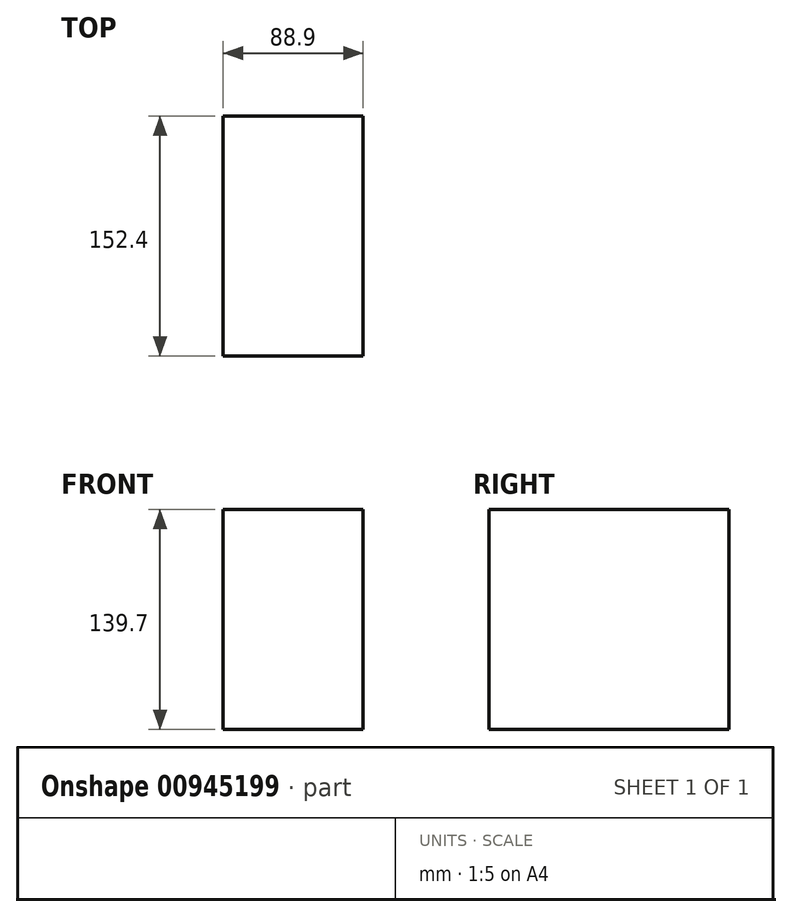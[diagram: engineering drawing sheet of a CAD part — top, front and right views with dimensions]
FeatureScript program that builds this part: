
annotation { "Feature Type Name" : "Feature", "Feature Type Description" : "" }
export const myFeature = defineFeature(function(context is Context, id is Id, definition is map)
    precondition{}
    {
        {
            var Q0;
            Q0=qCreatedBy(makeId("Top.planeOp"),FACE);
            var sketch = newSketch(context, id + "F0", { "sketchPlane" : qUnion([Q0])});
            skLineSegment(sketch, "E0.bottom", {"start": v(-171.68, 124.72) * mm, "end": v(-82.78, 124.72) * mm});
            skLineSegment(sketch, "E0.top", {"start": v(-171.68, -27.68) * mm, "end": v(-82.78, -27.68) * mm});
            skLineSegment(sketch, "E0.left", {"start": v(-171.68, 124.72) * mm, "end": v(-171.68, -27.68) * mm});
            skLineSegment(sketch, "E0.right", {"start": v(-82.78, 124.72) * mm, "end": v(-82.78, -27.68) * mm});
            skSolve(sketch);
        }
        {
            var Q0;
            Q0=makeQuery(id+"F0.imprint","IMPRINT",FACE,{"disambiguationData":[TD([[makeQuery(id+"F0.imprint","IMPRINT",EDGE,{"derivedFrom":sQuery(id+"F0.wireOp",EDGE,"E0.bottom")}),-1.0]])]});
            extrude(context, id + "F1", {"entities" : qUnion([Q0]), "depth" : 139.7 * mm, "offsetDistance" : 25.4 * mm});
        }
    });
